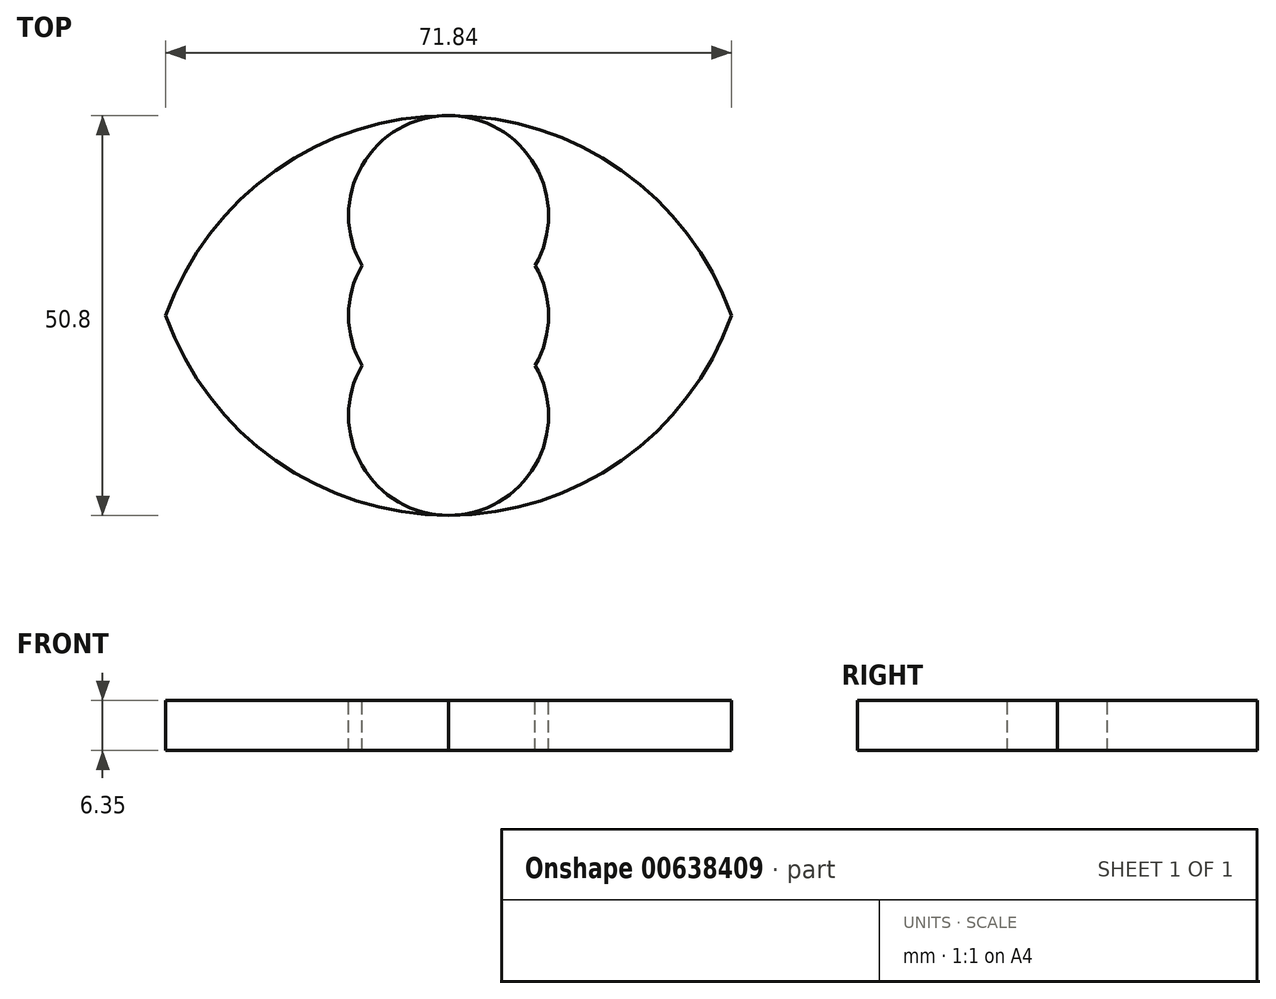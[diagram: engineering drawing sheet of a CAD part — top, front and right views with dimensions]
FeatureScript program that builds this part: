
annotation { "Feature Type Name" : "Feature", "Feature Type Description" : "" }
export const myFeature = defineFeature(function(context is Context, id is Id, definition is map)
    precondition{}
    {
        {
            var Q0;
            Q0=qCreatedBy(makeId("Top.planeOp"),FACE);
            var sketch = newSketch(context, id + "F0", { "sketchPlane" : qUnion([Q0])});
            skCircle(sketch, "E0", {"center": v(0, 0) * mm, "radius": 38.1 * mm});
            skCircle(sketch, "E1", {"center": v(0, 0) * mm, "radius": 12.7 * mm});
            skLineSegment(sketch, "E2", {"start": v(0, 0) * mm, "end": v(0, -38.1) * mm});
            skLineSegment(sketch, "E3", {"start": v(0, -38.1) * mm, "end": v(0, -38.1) * mm});
            skLineSegment(sketch, "E4", {"start": v(0, 0) * mm, "end": v(0, 38.1) * mm});
            skCircle(sketch, "E5", {"center": v(0, -12.7) * mm, "radius": 12.7 * mm});
            skCircle(sketch, "E6", {"center": v(0, -12.7) * mm, "radius": 38.1 * mm});
            skLineSegment(sketch, "E7", {"start": v(0, -38.1) * mm, "end": v(0, -50.8) * mm});
            skCircle(sketch, "E8", {"center": v(0, -25.4) * mm, "radius": 12.7 * mm});
            skCircle(sketch, "E9", {"center": v(0, -25.4) * mm, "radius": 38.1 * mm});
            skLineSegment(sketch, "E10", {"start": v(0, -50.8) * mm, "end": v(0, -63.5) * mm});
            skLineSegment(sketch, "E11", {"start": v(0, -63.5) * mm, "end": v(0, 12.7) * mm});
            skLineSegment(sketch, "E12", {"start": v(0, 12.7) * mm, "end": v(0, 25.4) * mm});
            skSolve(sketch);
        }
        {
            var Q0;
            {var subQ0=sQuery(id+"F0.wireOp",EDGE,"E2");var subQ1=sQuery(id+"F0.wireOp",EDGE,"E0");var subQ2=makeQuery(id+"F0.imprint","INTERSECT",VERTEX,{"derivedFrom":[subQ1,subQ0]});Q0=makeQuery(id+"F0.imprint","IMPRINT",FACE,{"disambiguationData":[TD([[makeQuery(id+"F0.imprint","IMPRINT",EDGE,{"disambiguationData":[TD([[subQ2,-1.0]])],"derivedFrom":subQ1}),1.0]])]});}
            var Q1;
            {var subQ0=sQuery(id+"F0.wireOp",EDGE,"E2");var subQ1=sQuery(id+"F0.wireOp",EDGE,"E0");var subQ2=makeQuery(id+"F0.imprint","INTERSECT",VERTEX,{"derivedFrom":[subQ1,subQ0]});Q1=makeQuery(id+"F0.imprint","IMPRINT",FACE,{"disambiguationData":[TD([[makeQuery(id+"F0.imprint","IMPRINT",EDGE,{"disambiguationData":[TD([[subQ2,1.0]])],"derivedFrom":subQ1}),1.0]])]});}
            extrude(context, id + "F1", {"entities" : qUnion([Q0, Q1]), "oppositeDirection" : true, "depth" : 6.35 * mm, "offsetDistance" : 25.4 * mm});
        }
    });
